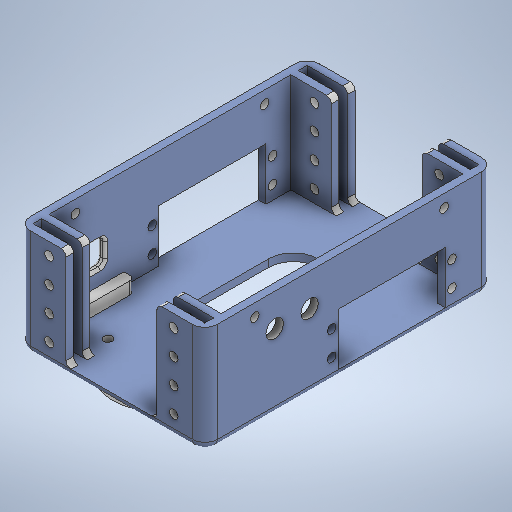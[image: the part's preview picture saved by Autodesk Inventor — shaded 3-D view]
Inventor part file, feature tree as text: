
AUTODESK INVENTOR PART (.ipt)
format: ipt  version: 2025 (Build 290162000, 162)  size: 1,123,840 bytes
history: native  units: mm
features: extrude x10, sketch x10, fillet x8
ambient origin geometry x8: Origin, YZ Plane, XZ Plane, XY Plane, X Axis, Y Axis, Z Axis, Center Point
bodies: Solide1 (feature_tree)
feature tree (28):
  extrude  "Extrusion1"  Depth=3.0mm TaperAngle=0.0deg
  extrude  "Extrusion2"  Depth=3.0mm
  extrude  "Extrusion3"  Depth=40.0mm TaperAngle=0.0deg
  fillet  "Congé1"  Radius=3.0mm
  fillet  "Congé2"  Radius=3.0mm
  extrude  "Extrusion5"  Depth=100.0mm TaperAngle=0.0deg
  fillet  "Congé5"  Radius=43.0mm
  extrude  "Extrusion6"  Depth=21.0mm
  fillet  "Congé6"  Radius=75.0mm
  fillet  "Congé7"  Radius=116.0mm
  extrude  "Extrusion7"  Depth=5.0mm
  extrude  "Extrusion8"  Depth=3.0mm
  extrude  "Extrusion9"  Depth=3.5mm
  fillet  "Congé8"  Radius=60.0mm
  fillet  "Congé9"  Radius=30.0mm
  extrude  "Extrusion10"  Depth=3.0mm TaperAngle=0.0deg
  extrude  "Extrusion11"  Depth=10.0mm
  fillet  "Congé10"  Radius=18.25mm
  sketch  "Esquisse1"
  sketch  "Esquisse2"
  sketch  "Esquisse3"
  sketch  "Esquisse5"
  sketch  "Esquisse6"
  sketch  "Esquisse7"
  sketch  "Esquisse8"
  sketch  "Esquisse9"
  sketch  "Esquisse10"
  sketch  "Esquisse11"
